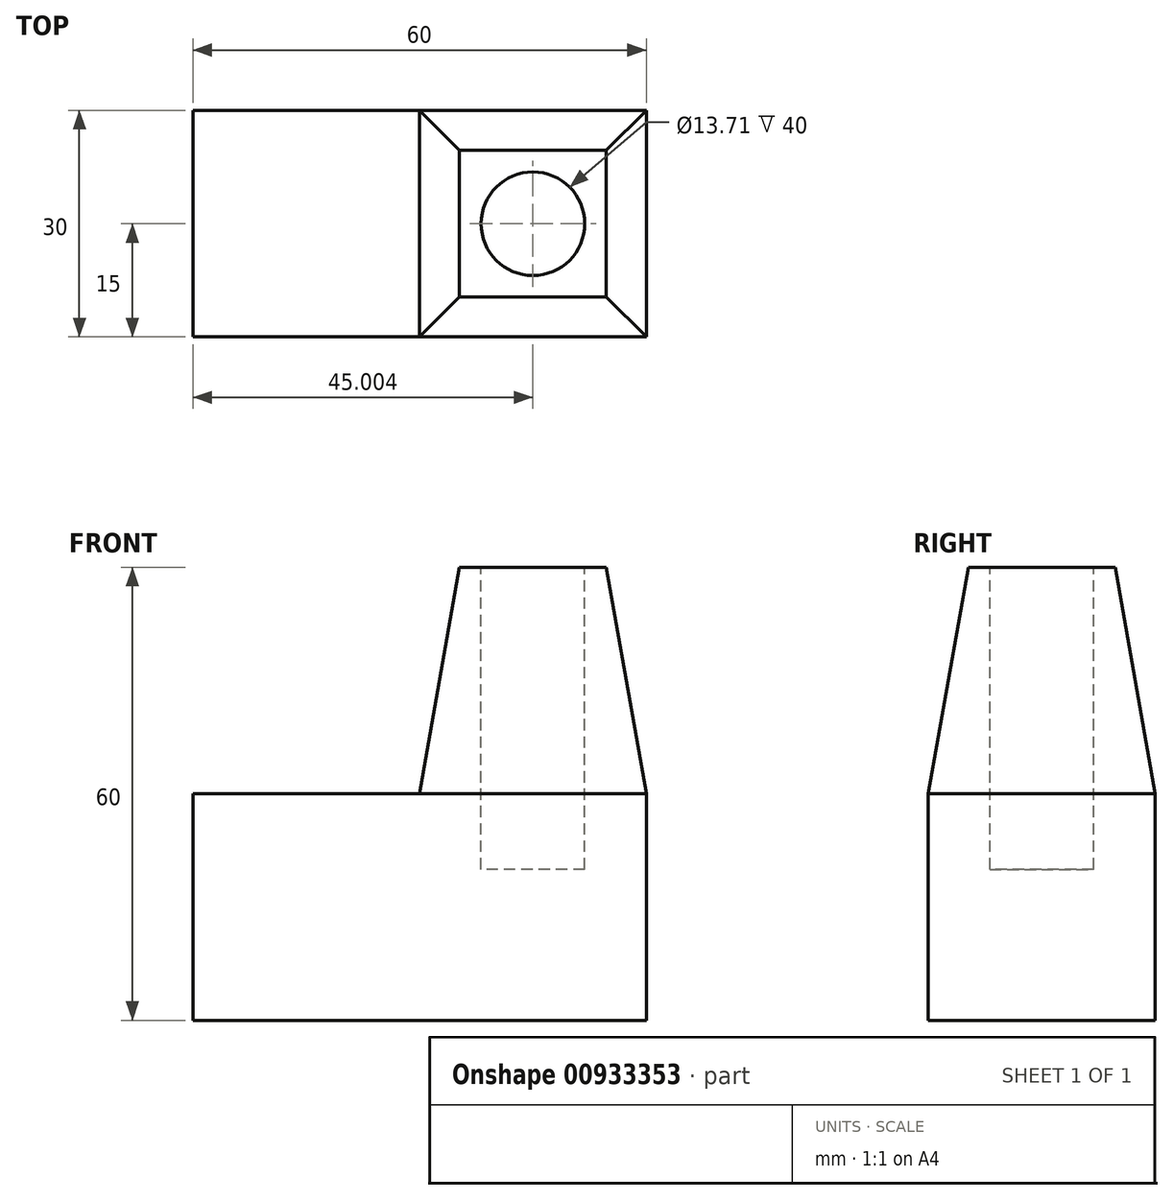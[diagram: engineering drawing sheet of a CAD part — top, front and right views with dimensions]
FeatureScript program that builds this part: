
annotation { "Feature Type Name" : "Feature", "Feature Type Description" : "" }
export const myFeature = defineFeature(function(context is Context, id is Id, definition is map)
    precondition{}
    {
        {
            var Q0;
            Q0=qCreatedBy(makeId("Front.planeOp"),FACE);
            var sketch = newSketch(context, id + "F0", { "sketchPlane" : qUnion([Q0])});
            skLineSegment(sketch, "E0.bottom", {"start": v(-31.96, 16.82) * mm, "end": v(28.04, 16.82) * mm});
            skLineSegment(sketch, "E0.top", {"start": v(-31.96, -13.18) * mm, "end": v(28.04, -13.18) * mm});
            skLineSegment(sketch, "E0.left", {"start": v(-31.96, 16.82) * mm, "end": v(-31.96, -13.18) * mm});
            skLineSegment(sketch, "E0.right", {"start": v(28.04, 16.82) * mm, "end": v(28.04, -13.18) * mm});
            skSolve(sketch);
        }
        {
            var Q0;
            Q0=makeQuery(id+"F0.imprint","IMPRINT",FACE,{"disambiguationData":[TD([[makeQuery(id+"F0.imprint","IMPRINT",EDGE,{"derivedFrom":sQuery(id+"F0.wireOp",EDGE,"E0.bottom")}),-1.0]])]});
            extrude(context, id + "F1", {"entities" : qUnion([Q0]), "depth" : 30 * mm, "offsetDistance" : 25.4 * mm});
        }
        {
            var Q0;
            Q0=makeQuery(id+"F1.opExtrude","SWEPT_FACE",FACE,{"disambiguationData":[OSD([sQuery(id+"F0.wireOp",EDGE,"E0.bottom")])]});
            var sketch = newSketch(context, id + "F2", { "sketchPlane" : qUnion([Q0])});
            skLineSegment(sketch, "E1.bottom", {"start": v(28.04, 0) * mm, "end": v(-1.96, 0) * mm});
            skLineSegment(sketch, "E1.top", {"start": v(28.04, -30) * mm, "end": v(-1.96, -30) * mm});
            skLineSegment(sketch, "E1.left", {"start": v(28.04, 0) * mm, "end": v(28.04, -30) * mm});
            skLineSegment(sketch, "E1.right", {"start": v(-1.96, 0) * mm, "end": v(-1.96, -30) * mm});
            skSolve(sketch);
        }
        {
            var Q0;
            Q0=makeQuery(id+"F2.imprint","IMPRINT",FACE,{"disambiguationData":[TD([[makeQuery(id+"F2.imprint","IMPRINT",EDGE,{"derivedFrom":sQuery(id+"F2.wireOp",EDGE,"E1.bottom")}),-1.0]])]});
            extrude(context, id + "F3", {"entities" : qUnion([Q0]), "operationType" : NewBodyOperationType.ADD, "depth" : 30 * mm, "offsetDistance" : 25.4 * mm, "hasDraft" : true, "draftAngle" : 10 * degree, "draftPullDirection" : true});
        }
        {
            var Q0;
            Q0=makeQuery(id+"F3.opExtrude","CAP_FACE",FACE,{"disambiguationData":[OSD([sQuery(id+"F2.wireOp",EDGE,"E1.bottom"),sQuery(id+"F2.wireOp",EDGE,"E1.top"),sQuery(id+"F2.wireOp",EDGE,"E1.left"),sQuery(id+"F2.wireOp",EDGE,"E1.right")])],"isStart":false});
            var sketch = newSketch(context, id + "F4", { "sketchPlane" : qUnion([Q0])});
            skCircle(sketch, "E2", {"center": v(13.04, -15) * mm, "radius": 6.86 * mm});
            skPoint(sketch, "E2.centerSnap0", {"position": v(3.33, -15) * mm});
            skPoint(sketch, "E2.centerSnap1", {"position": v(13.04, -5.29) * mm});
            skSolve(sketch);
        }
        {
            var Q0;
            Q0=makeQuery(id+"F4.imprint","IMPRINT",FACE,{"disambiguationData":[TD([[makeQuery(id+"F4.imprint","IMPRINT",EDGE,{"derivedFrom":sQuery(id+"F4.wireOp",EDGE,"E2")}),1.0]])]});
            extrude(context, id + "F5", {"entities" : qUnion([Q0]), "operationType" : NewBodyOperationType.REMOVE, "oppositeDirection" : true, "depth" : 40 * mm, "offsetDistance" : 25.4 * mm});
        }
    });
